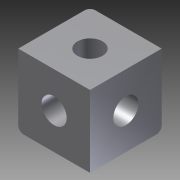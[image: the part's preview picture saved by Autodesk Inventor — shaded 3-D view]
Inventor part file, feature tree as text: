
AUTODESK INVENTOR PART (.ipt)
format: ipt  version: 2012 (Build 160160000, 160)  size: 115,712 bytes
history: native  units: mm
features: extrude x3, sketch x3, fillet x1
ambient origin geometry x8: Origin, YZ Plane, XZ Plane, XY Plane, X Axis, Y Axis, Z Axis, Center Point
bodies: Solid1 (feature_tree)
feature tree (7):
  extrude  "Extrusion1"  Depth=20.0mm
  extrude  "Extrusion2"  Depth=20.0mm TaperAngle=0.0deg
  extrude  "Extrusion3"  Depth=20.0mm TaperAngle=0.0deg
  fillet  "Fillet1"  Radius=7.0mm
  sketch  "Sketch1"  dims[d0=20.0mm d1=20.0mm]
  sketch  "Sketch2"  dims[d2=7.0mm d3=20.0mm d4=0.0mm]
  sketch  "Sketch3"  dims[d5=7.0mm d6=20.0mm d7=0.0mm d8=7.0mm d9=20.0mm d10=0.0mm d11=1.5mm]
